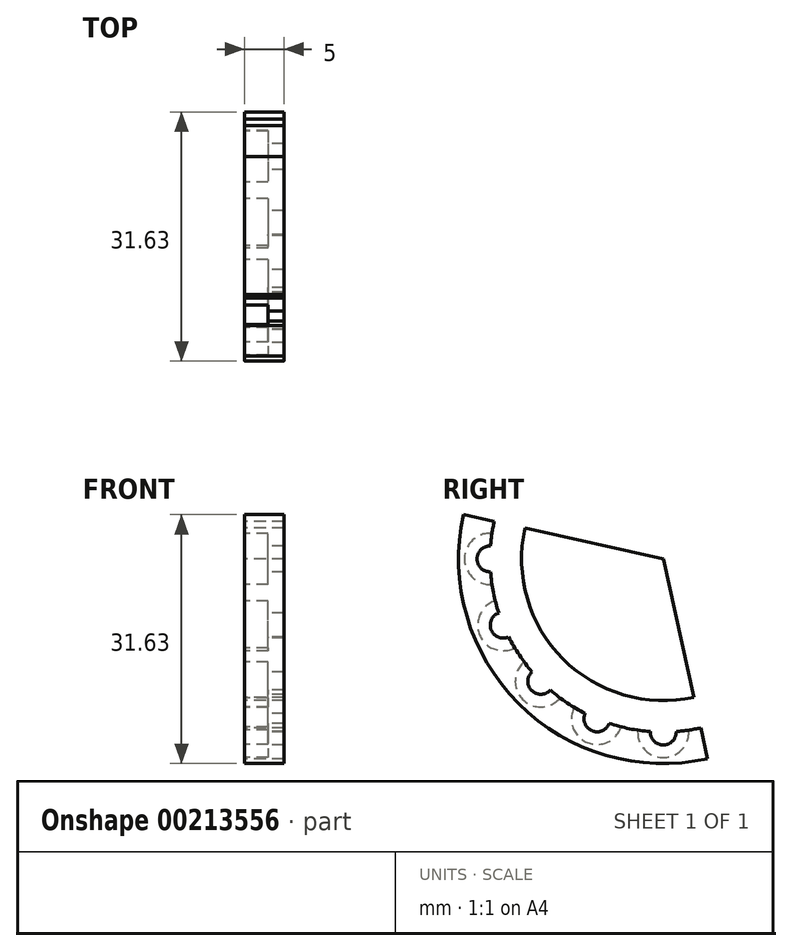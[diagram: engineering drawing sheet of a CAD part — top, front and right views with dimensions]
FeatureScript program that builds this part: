
annotation { "Feature Type Name" : "Feature", "Feature Type Description" : "" }
export const myFeature = defineFeature(function(context is Context, id is Id, definition is map)
    precondition{}
    {
        {
            var Q0;
            Q0=qCreatedBy(makeId("Right.planeOp"),FACE);
            var sketch = newSketch(context, id + "F0", { "sketchPlane" : qUnion([Q0])});
            skArc(sketch, "E0", {"start": v(-25.38, 5.63) * mm, "mid": v(-18.38, -18.38) * mm, "end": v(5.63, -25.38) * mm});
            skLineSegment(sketch, "E1", {"start": v(0, 0) * mm, "end": v(5.63, -25.38) * mm});
            skLineSegment(sketch, "E2", {"start": v(0, 0) * mm, "end": v(-25.38, 5.63) * mm});
            skArc(sketch, "E3", {"start": v(-21.48, 4.76) * mm, "mid": v(-15.56, -15.56) * mm, "end": v(4.76, -21.48) * mm});
            skPoint(sketch, "E4", {"position": v(-22, 0) * mm});
            skPoint(sketch, "E5", {"position": v(0, -22) * mm});
            skArc(sketch, "E6", {"start": v(-22, 0) * mm, "mid": v(-20.33, -8.42) * mm, "end": v(-15.56, -15.56) * mm});
            skArc(sketch, "E7", {"start": v(-22, 0) * mm, "mid": v(-21.58, -4.3) * mm, "end": v(-20.33, -8.42) * mm});
            skArc(sketch, "E8", {"start": v(-15.56, -15.56) * mm, "mid": v(-8.42, -20.33) * mm, "end": v(0, -22) * mm});
            skArc(sketch, "E9", {"start": v(-15.56, -15.56) * mm, "mid": v(-12.22, -18.3) * mm, "end": v(-8.42, -20.33) * mm});
            skArc(sketch, "E10", {"start": v(-17.57, 3.9) * mm, "mid": v(-12.73, -12.73) * mm, "end": v(3.9, -17.57) * mm});
            skArc(sketch, "E11", {"start": v(-3.9, 0.87) * mm, "mid": v(2.83, 2.83) * mm, "end": v(0.87, -3.9) * mm});
            skLineSegment(sketch, "E12", {"start": v(0, 0) * mm, "end": v(-15.56, -15.56) * mm, "construction": true});
            skLineSegment(sketch, "E13", {"start": v(0, 0) * mm, "end": v(-31.17, 0) * mm, "construction": true});
            skLineSegment(sketch, "E14", {"start": v(-20.33, -8.42) * mm, "end": v(0, 0) * mm, "construction": true});
            skLineSegment(sketch, "E15", {"start": v(-8.42, -20.33) * mm, "end": v(0, 0) * mm, "construction": true});
            skLineSegment(sketch, "E16", {"start": v(0, -22) * mm, "end": v(0, 0) * mm, "construction": true});
            skSolve(sketch);
        }
        {
            var Q0;
            {var subQ4=sQuery(id+"F0.wireOp",EDGE,"E0");Q0=makeQuery(id+"F0.imprint","IMPRINT",FACE,{"disambiguationData":[TD([[makeQuery(id+"F0.imprint","IMPRINT",EDGE,{"derivedFrom":subQ4}),1.0]])]});}
            var Q1;
            Q1=makeQuery(id+"F0.imprint","IMPRINT",FACE,{"disambiguationData":[TD([[makeQuery(id+"F0.imprint","IMPRINT",EDGE,{"derivedFrom":sQuery(id+"F0.wireOp",EDGE,"E6")}),1.0]])]});
            var Q2;
            {var subQ0=sQuery(id+"F0.wireOp",EDGE,"E10");Q2=makeQuery(id+"F0.imprint","IMPRINT",FACE,{"disambiguationData":[TD([[makeQuery(id+"F0.imprint","IMPRINT",EDGE,{"derivedFrom":subQ0}),1.0]])]});}
            var Q3;
            {var subQ3=sQuery(id+"F0.wireOp",EDGE,"E11");Q3=makeQuery(id+"F0.imprint","IMPRINT",FACE,{"disambiguationData":[TD([[makeQuery(id+"F0.imprint","IMPRINT",EDGE,{"derivedFrom":subQ3}),-1.0]])]});}
            extrude(context, id + "F1", {"entities" : qUnion([Q0, Q1, Q2, Q3]), "depth" : 5 * mm});
        }
        {
            var Q0;
            Q0=sQuery(id+"F0.wireOp",VERTEX,"E4");
            var Q1;
            Q1=sQuery(id+"F0.wireOp",VERTEX,"E7.end");
            var Q2;
            Q2=sQuery(id+"F0.wireOp",VERTEX,"E9.start");
            var Q3;
            Q3=sQuery(id+"F0.wireOp",VERTEX,"E9.end");
            var Q4;
            Q4=sQuery(id+"F0.wireOp",VERTEX,"E5");
            var Q5;
            Q5=sQuery(id+"F0.wireOp",VERTEX,"E7.center");
            var Q6;
            Q6=makeQuery(id+"F1.opExtrude","SWEPT_BODY",BODY,{"disambiguationData":[OSD([sQuery(id+"F0.wireOp",EDGE,"E0"),sQuery(id+"F0.wireOp",EDGE,"E1"),sQuery(id+"F0.wireOp",EDGE,"E2")])]});
            hole(context, id + "F2", {"style" : HoleStyle.C_BORE, "endStyle" : HoleEndStyle.THROUGH, "oppositeDirection" : true, "standardTappedOrClearance" : lookupTablePath({ "standard" : "ISO", "fit" : "Normal", "size" : "M3", "type" : "Clearance" }), "standardBlindInLast" : lookupTablePath({ "fit" : "Standard", "standard" : "ISO", "size" : "M3", "type" : "Clearance" }), "holeDiameter" : 3.3 * mm, "cBoreDiameter" : 6.5 * mm, "cBoreDepth" : 3 * mm, "locations" : qUnion([Q0, Q1, Q2, Q3, Q4, Q5]), "scope" : qUnion([Q6]), "isTappedThrough" : true});
        }
    });
